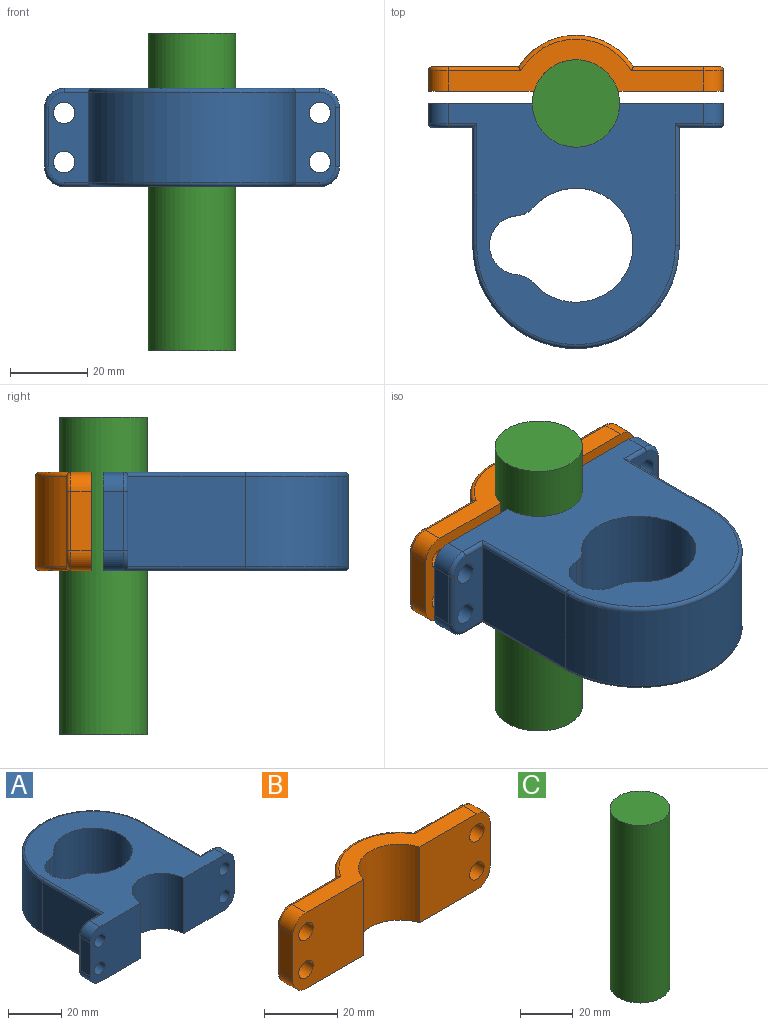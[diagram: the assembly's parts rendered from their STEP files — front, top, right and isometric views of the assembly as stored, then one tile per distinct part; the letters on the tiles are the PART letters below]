
ASSEMBLY  parts=3 mates=3
PART A: 40 faces, bbox 77x65.6x26.2 mm
  f0: plane 66.04x62.36mm, normal (0,0,1), area 2008.9mm2, adj f4,f5,f6,f16,f17,f18,f19,f22
  f1: plane 66.04x62.36mm, normal (0,0,-1), area 2008.9mm2, adj f4,f5,f6,f16,f17,f18,f19,f20
  f2: plane 23.37x10.41mm, normal (0,1,0), area 187.2mm2, adj f11,f14,f15,f31,f33,f35,f37,f39
  f3: plane 15.24x5.33mm, normal (-1,0,0), area 81.3mm2, adj f4,f21,f23,f35
  f4: plane 26.8x25.4mm, normal (0,-1,0), area 620.5mm2, adj f0,f1,f3,f5,f14,f15,f21,f23
  f5: cylinder r=11.3mm len=25.4mm, axis (0,0,-1), area 901.9mm2, adj f0,f1,f4,f6
  f6: plane 26.8x25.4mm, normal (0,-1,0), area 620.5mm2, adj f0,f1,f5,f7,f12,f13,f20,f22
  f7: plane 15.24x5.33mm, normal (1,0,0), area 81.3mm2, adj f6,f20,f22,f28
  f8: plane 23.37x10.41mm, normal (0,1,0), area 187.2mm2, adj f9,f12,f13,f24,f26,f28,f30,f32
  f9: plane 30.35x23.37mm, normal (1,0,0), area 709.3mm2, adj f8,f10,f25,f34
  f10: cylinder r=26.67mm len=53.34mm, axis (0,0,-1), area 1957.9mm2, adj f9,f11,f27,f36
  f11: plane 30.35x23.37mm, normal (-1,0,0), area 709.3mm2, adj f2,f10,f29,f38
  f12: cylinder r=2.79mm len=6.35mm, axis (0,1,0), area 111.5mm2, adj f6,f8
  f13: cylinder r=2.79mm len=6.35mm, axis (0,1,0), area 111.5mm2, adj f6,f8
  f14: cylinder r=2.79mm len=6.35mm, axis (0,1,0), area 111.5mm2, adj f2,f4
  f15: cylinder r=2.79mm len=6.35mm, axis (0,1,0), area 111.5mm2, adj f2,f4
  f16: cylinder r=6.35mm len=25.4mm, axis (0,0,1), area 124.3mm2, adj f0,f1,f17,f19
  f17: cylinder r=7.62mm len=25.4mm, axis (0,0,1), area 577.7mm2, adj f0,f1,f16,f18
  f18: cylinder r=6.35mm len=25.4mm, axis (0,0,1), area 124.3mm2, adj f0,f1,f17,f19
  f19: cylinder r=14.73mm len=29.46mm, axis (0,0,1), area 1811.1mm2, adj f0,f1,f16,f18
  f20: cylinder r=5.08mm len=5.33mm, axis (0,1,0), area 42.6mm2, adj f1,f6,f7,f26
  f21: cylinder r=5.08mm len=5.33mm, axis (0,-1,0), area 42.6mm2, adj f1,f3,f4,f33
  f22: cylinder r=5.08mm len=5.33mm, axis (0,-1,0), area 42.6mm2, adj f0,f6,f7,f30
  f23: cylinder r=5.08mm len=5.33mm, axis (0,1,0), area 42.6mm2, adj f0,f3,f4,f37
  f24: cylinder r=1.02mm len=7.37mm, axis (-1,0,0), area 10.7mm2, adj f1,f8,f25,f26
  f25: cylinder r=1.02mm len=31.37mm, axis (0,1,0), area 49mm2, adj f1,f9,f24,f27
  f26: torus R=4.06mm, axis (0,1,0), area 11.8mm2, adj f8,f20,f24,f28
  f27: torus R=25.65mm, axis (0,0,1), area 131.9mm2, adj f1,f10,f25,f29
  f28: cylinder r=1.02mm len=15.24mm, axis (0,0,-1), area 24.3mm2, adj f7,f8,f26,f30
  f29: cylinder r=1.02mm len=31.37mm, axis (0,-1,0), area 49mm2, adj f1,f11,f27,f31
  f30: torus R=4.06mm, axis (0,1,0), area 11.8mm2, adj f8,f22,f28,f32
  f31: cylinder r=1.02mm len=7.37mm, axis (-1,0,0), area 10.7mm2, adj f1,f2,f29,f33
  f32: cylinder r=1.02mm len=7.37mm, axis (1,0,0), area 10.7mm2, adj f0,f8,f30,f34
  f33: torus R=4.06mm, axis (0,1,0), area 11.8mm2, adj f2,f21,f31,f35
  f34: cylinder r=1.02mm len=31.37mm, axis (0,-1,0), area 49mm2, adj f0,f9,f32,f36
  f35: cylinder r=1.02mm len=15.24mm, axis (0,0,-1), area 24.3mm2, adj f2,f3,f33,f37
  f36: torus R=25.65mm, axis (0,0,1), area 131.9mm2, adj f0,f10,f34,f38
  f37: torus R=4.06mm, axis (0,1,0), area 11.8mm2, adj f2,f23,f35,f39
  f38: cylinder r=1.02mm len=31.37mm, axis (0,1,0), area 49mm2, adj f0,f11,f36,f39
  f39: cylinder r=1.02mm len=7.37mm, axis (1,0,0), area 10.7mm2, adj f0,f2,f37,f38
PART B: 30 faces, bbox 77x15.9x26.2 mm
  f0: plane 15.24x5.33mm, normal (-1,0,0), area 81.3mm2, adj f1,f15,f17,f22
  f1: plane 27.27x25.4mm, normal (0,-1,0), area 632.4mm2, adj f0,f2,f8,f9,f10,f11,f15,f17
  f2: cylinder r=11.29mm len=25.4mm, axis (0,0,-1), area 737.4mm2, adj f1,f3,f8,f9
  f3: plane 27.27x25.4mm, normal (0,-1,0), area 632.4mm2, adj f2,f4,f8,f9,f12,f13,f14,f16
  f4: plane 15.24x5.33mm, normal (1,0,0), area 81.3mm2, adj f3,f14,f16,f25
  f5: plane 23.37x22.24mm, normal (0,1,0), area 463.5mm2, adj f6,f12,f13,f21,f23,f25,f27,f29
  f6: cylinder r=17.64mm len=29.7mm, axis (0,0,-1), area 824.8mm2, adj f5,f7,f19,f28
  f7: plane 23.37x22.24mm, normal (0,1,0), area 463.5mm2, adj f6,f10,f11,f18,f20,f22,f24,f26
  f8: plane 66.04x13.45mm, normal (0,0,1), area 386.9mm2, adj f1,f2,f3,f16,f17,f18,f19,f21
  f9: plane 66.04x13.45mm, normal (0,0,-1), area 386.9mm2, adj f1,f2,f3,f14,f15,f26,f28,f29
  f10: cylinder r=2.79mm len=6.35mm, axis (0,1,0), area 111.5mm2, adj f1,f7
  f11: cylinder r=2.79mm len=6.35mm, axis (0,1,0), area 111.5mm2, adj f1,f7
  f12: cylinder r=2.79mm len=6.35mm, axis (0,1,0), area 111.5mm2, adj f3,f5
  f13: cylinder r=2.79mm len=6.35mm, axis (0,1,0), area 111.5mm2, adj f3,f5
  f14: cylinder r=5.08mm len=5.33mm, axis (0,1,0), area 42.6mm2, adj f3,f4,f9,f27
  f15: cylinder r=5.08mm len=5.33mm, axis (0,-1,0), area 42.6mm2, adj f0,f1,f9,f24
  f16: cylinder r=5.08mm len=5.33mm, axis (0,-1,0), area 42.6mm2, adj f3,f4,f8,f23
  f17: cylinder r=5.08mm len=5.33mm, axis (0,1,0), area 42.6mm2, adj f0,f1,f8,f20
  f18: cylinder r=1.02mm len=18.74mm, axis (1,0,0), area 29.3mm2, adj f7,f8,f19,f20
  f19: torus R=16.62mm, axis (0,0,1), area 55.8mm2, adj f6,f8,f18,f21
  f20: torus R=4.06mm, axis (0,-1,0), area 11.8mm2, adj f7,f17,f18,f22
  f21: cylinder r=1.02mm len=18.74mm, axis (1,0,0), area 29.3mm2, adj f5,f8,f19,f23
  f22: cylinder r=1.02mm len=15.24mm, axis (0,0,-1), area 24.3mm2, adj f0,f7,f20,f24
  f23: torus R=4.06mm, axis (0,-1,0), area 11.8mm2, adj f5,f16,f21,f25
  f24: torus R=4.06mm, axis (0,-1,0), area 11.8mm2, adj f7,f15,f22,f26
  f25: cylinder r=1.02mm len=15.24mm, axis (0,0,-1), area 24.3mm2, adj f4,f5,f23,f27
  f26: cylinder r=1.02mm len=18.74mm, axis (-1,0,0), area 29.3mm2, adj f7,f9,f24,f28
  f27: torus R=4.06mm, axis (0,-1,0), area 11.8mm2, adj f5,f14,f25,f29
  f28: torus R=16.62mm, axis (0,0,1), area 55.8mm2, adj f6,f9,f26,f29
  f29: cylinder r=1.02mm len=18.74mm, axis (-1,0,0), area 29.3mm2, adj f5,f9,f27,f28
PART C: 3 faces, bbox 22.6x22.6x82 mm
  f0: cylinder r=11.29mm len=82.04mm, axis (0,0,-1), area 5820mm2, adj f1,f2
  f1: plane 22.58x22.58mm, normal (0,0,1), area 400.5mm2, adj f0
  f2: plane 22.58x22.58mm, normal (0,0,-1), area 400.5mm2, adj f0
PLACE A rot(axis=(1,0,0),180deg) t=(8.45,0.78,38.43)mm
PLACE B t=(8.45,10.19,13.03)mm
PLACE C t=(8.45,7.01,-29.38)mm
MATE slider A.f13 <-> B.f13  axis (0,-1,0) through (41.47,0.78,32.08)mm
MATE slider C.f0 <-> B.f2  axis (0,0,1) through (8.45,7.01,52.66)mm
MATE parallel A.f15 <-> B.f10  axis (0,1,0) through (-24.57,7.13,19.38)mm
